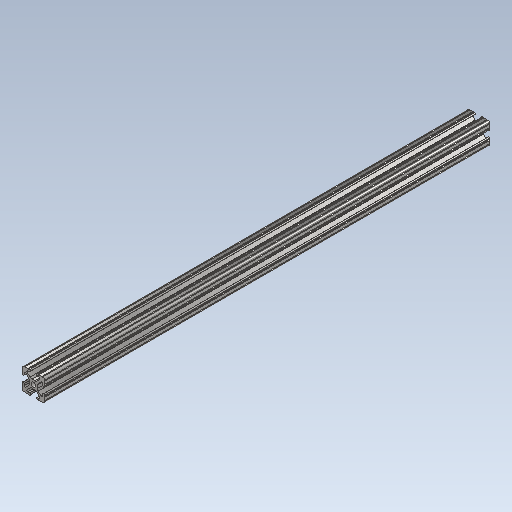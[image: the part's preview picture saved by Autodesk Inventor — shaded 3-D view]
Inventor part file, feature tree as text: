
AUTODESK INVENTOR PART (.ipt)
format: ipt  version: 2020 (Build 240168000, 168)  size: 241,664 bytes
history: native  units: in
note: dims shown in document units (in); Inventor stores cm internally (conversion verified against a paired STEP export)
features: extrude x1, sketch x1
ambient origin geometry x8: Origin, YZ Plane, XZ Plane, XY Plane, X Axis, Y Axis, Z Axis, Center Point
bodies: Solid1 (feature_tree)
feature tree (2):
  extrude  "Extrusion1"  [1 undecoded]
  sketch  "Sketch1"  dims[d0=20.0in d1=0.0in]
note: 1 required parameter value undecoded (feature->parameter linkage not recoverable at this tier; creation-order binding heuristic only, values carry confidence <= 0.55)
